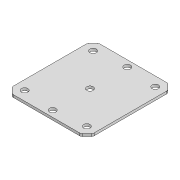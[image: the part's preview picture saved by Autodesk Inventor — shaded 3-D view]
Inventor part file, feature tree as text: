
AUTODESK INVENTOR PART (.ipt)
format: ipt  version: 2020 (Build 240168000, 168)  size: 134,656 bytes
history: native  units: mm
features: sketch x3, hole x2, other x1, extrude x1, chamfer x1, fillet x1, projected_geometry x1
ambient origin geometry x8: Origin, YZ Plane, XZ Plane, XY Plane, X Axis, Y Axis, Z Axis, Center Point
bodies: Body1 (feature_tree)
feature tree (10):
  other  "ソリッド1"
  extrude  "押し出し1"  Depth=65.0mm
  hole  "穴1"  [1 undecoded]
  chamfer  "面取り1"  Distance=2.0mm
  fillet  "フィレット3"  Radius=50.0mm
  hole  "穴3"  [1 undecoded]
  sketch  "スケッチ1"
  sketch  "スケッチ2"
  sketch  "スケッチ5"
  projected_geometry  "投影ループ2"
note: 2 required parameter values undecoded (feature->parameter linkage not recoverable at this tier; creation-order binding heuristic only, values carry confidence <= 0.55)
